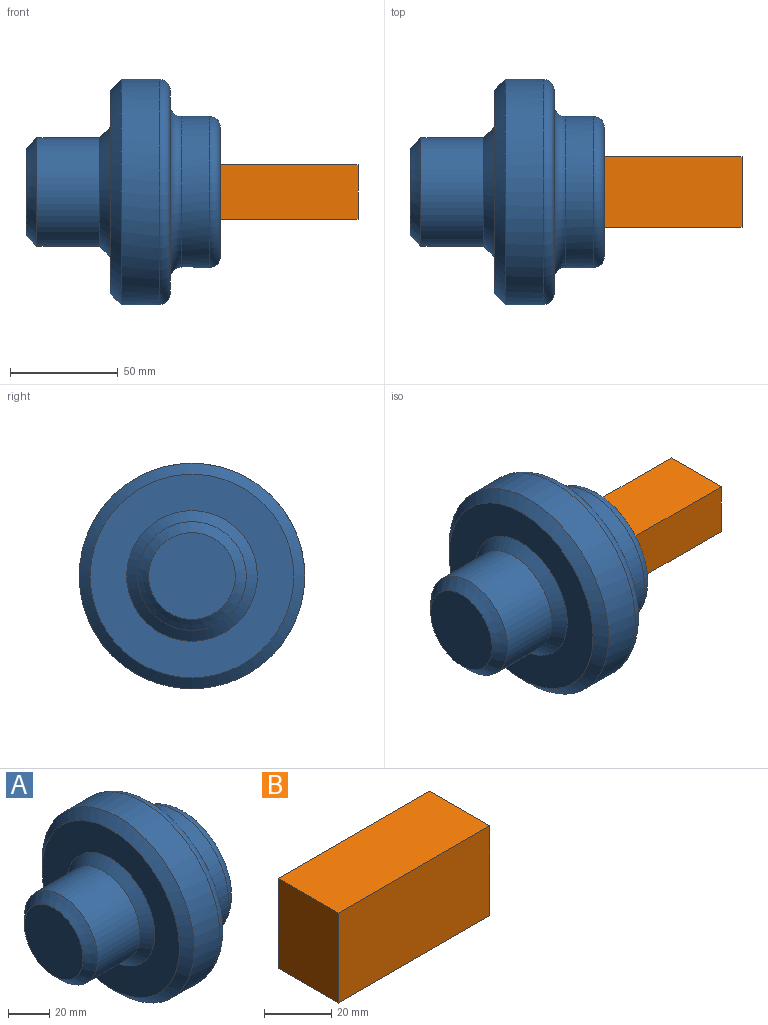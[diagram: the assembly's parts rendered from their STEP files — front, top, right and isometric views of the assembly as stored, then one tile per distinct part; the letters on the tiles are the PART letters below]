
ASSEMBLY  parts=2 mates=1
PART A: 13 faces, bbox 90.1x113.1x113.1 mm
  f0: plane 40.24x40.24mm, normal (-1,0,0), area 1271.9mm2, adj f7
  f1: cone r=0mm half-angle=89.6deg, axis (1,0,0), area 2814.7mm2, adj f10
  f2: cylinder r=35.05mm len=70.1mm, axis (-1,0,0), area 2880.2mm2, adj f10,f11
  f3: plane 94.38x94.38mm, normal (1,0,0), area 1935.8mm2, adj f11,f12
  f4: cylinder r=52.27mm len=104.54mm, axis (-1,0,0), area 5765.2mm2, adj f9,f12
  f5: plane 94.38x94.38mm, normal (-1,0,0), area 4114.7mm2, adj f8,f9
  f6: cylinder r=25.2mm len=50.4mm, axis (-1,0,0), area 4588.8mm2, adj f7,f8
  f7: cone r=20.12mm half-angle=45deg, axis (1,0,0), area 1022.9mm2, adj f0,f6
  f8: cone r=25.2mm half-angle=45deg, axis (1,0,0), area 1252.2mm2, adj f5,f6
  f9: cone r=47.19mm half-angle=45deg, axis (1,0,0), area 2244.7mm2, adj f4,f5
  f10: torus R=29.97mm, axis (1,0,0), area 1672.2mm2, adj f1,f2
  f11: torus R=40.13mm, axis (-1,0,0), area 1849.9mm2, adj f2,f3
  f12: torus R=47.19mm, axis (-1,0,0), area 2528mm2, adj f3,f4
PART B: 6 faces, bbox 63.9x25.4x32.8 mm
  f0: plane 63.87x25.4mm, normal (0,0,1), area 1622.3mm2, adj f1,f3,f4,f5
  f1: plane 32.8x25.4mm, normal (-1,0,0), area 833.2mm2, adj f0,f2,f4,f5
  f2: plane 63.87x25.4mm, normal (0,0,-1), area 1622.3mm2, adj f1,f3,f4,f5
  f3: plane 32.8x25.4mm, normal (1,0,0), area 833.2mm2, adj f0,f2,f4,f5
  f4: plane 63.87x32.8mm, normal (0,-1,0), area 2095.2mm2, adj f0,f1,f2,f3
  f5: plane 63.87x32.8mm, normal (0,1,0), area 2095.2mm2, adj f0,f1,f2,f3
PLACE A t=(22.52,9.21,6.36)mm fixed
PLACE B rot(axis=(0,-0.71,0.71),180deg) t=(206.19,182.13,-6.34)mm
MATE fastened A.f1 <-> B.f3  axis (1,0,0) through (66.87,9.21,6.36)mm
